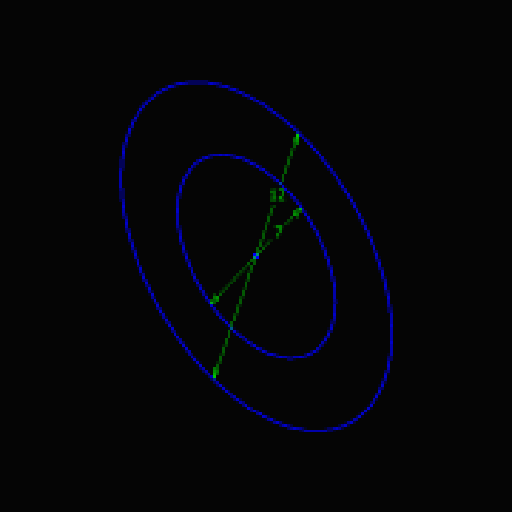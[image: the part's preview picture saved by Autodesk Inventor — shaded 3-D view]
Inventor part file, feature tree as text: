
AUTODESK INVENTOR PART (.ipt)
format: ipt  version: 2023.2 (Build 272271030, 271C)  size: 96,256 bytes
history: native  units: mm
features: extrude x2, sketch x2, projected_geometry x1
ambient origin geometry x8: Origin, YZ Plane, XZ Plane, XY Plane, X Axis, Y Axis, Z Axis, Center Point
bodies: Solid1 (feature_tree)
feature tree (5):
  extrude  "Extrusion1"  Depth=5.0mm
  extrude  "Extrusion2"  Depth=2.5mm
  sketch  "Sketch1"  dims[d0=10.0mm d1=5.0mm]
  sketch  "Sketch2"  dims[d2=5.0mm d3=0.0mm d4=0.5mm d5=2.5mm d6=0.0mm]
  projected_geometry  "Projected Loop1"
